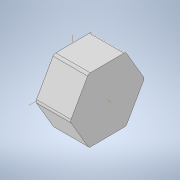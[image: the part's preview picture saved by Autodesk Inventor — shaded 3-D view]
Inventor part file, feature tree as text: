
AUTODESK INVENTOR PART (.ipt)
format: ipt  version: 2021.1 (Build 251245000, 245)  size: 113,664 bytes
history: native  units: in
note: dims shown in document units (in); Inventor stores cm internally (conversion verified against a paired STEP export)
features: extrude x1, sketch x1
ambient origin geometry x8: Origin, YZ Plane, XZ Plane, XY Plane, X Axis, Y Axis, Z Axis, Center Point
bodies: Solid1 (feature_tree)
feature tree (2):
  extrude  "Extrusion1"  Depth=0.5in
  sketch  "Sketch1"  dims[d0=10.6in d1=0.5in d2=5.7in d3=0.0in]
